# Revit family: LIRA Soap Bottle Holder - Single
name_source: partatom
category: Generic Models
units: mm (PartAtom-declared; Revit-internal decimal feet)

## family parameters
Always vertical = Yes
Can host rebar = No
Cut with Voids When Loaded = No
Maintain Annotation Orientation = No
OmniClass Number = 23.40.20.21.34
OmniClass Title = Soap Holders, Dispensers
Part Type = Normal
Room Calculation Point = No
Round Connector Dimension = Use Diameter
Shared = No
Work Plane-Based = No

## types (1)
- LIRA Soap bottle Holder - Single
    Catalog web link = https://www.abiinteriors.com.au
    Category = Accessories
    Default Elevation = 0 mm  [stored 0 ft]
    Description = Soap Bottle Holder
    Manufacturer = ABI Interiors Pty Ltd
    Material = Stainless Steel AISI 304
    Model = Brass(13522), Copper(12356), Nickel(13526), Gunmetal(12357), Black(13525), White(13527)
    Part Number = Brass(13522), Copper(12356), Nickel(13526), Gunmetal(12357), Black(13525), White(13527)
    Title = Lira Soap Bottle Holder
    URL = https://www.abiinteriors.com.au
    Volume = 0 m³

note: [stored X ft] marks values corroborated as IEEE doubles in the binary element streams (Revit-internal decimal feet)

## geometry (parser evidence)
native form markers: Sweep x3
no freeform markers — native parametric forms only
